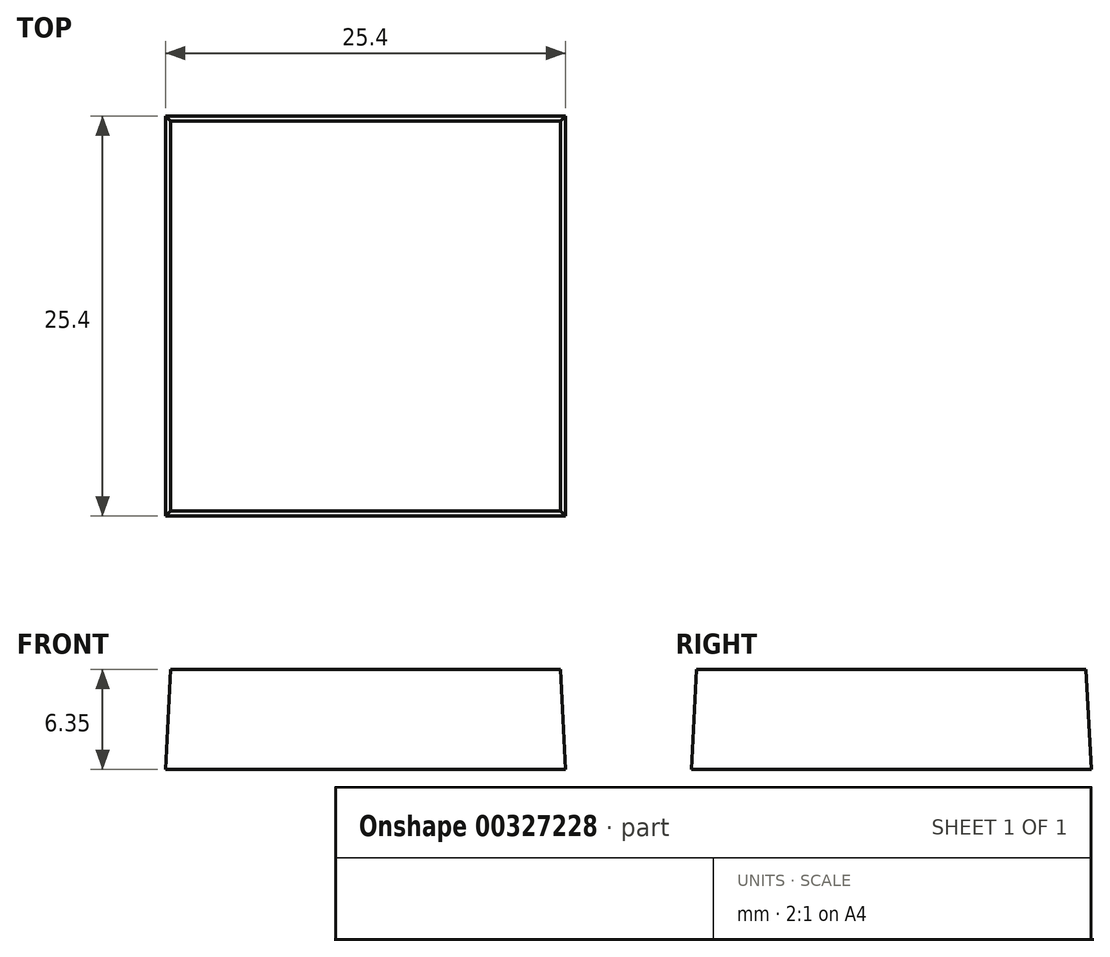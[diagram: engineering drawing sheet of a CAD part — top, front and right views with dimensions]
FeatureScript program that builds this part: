
annotation { "Feature Type Name" : "Feature", "Feature Type Description" : "" }
export const myFeature = defineFeature(function(context is Context, id is Id, definition is map)
    precondition{}
    {
        {
            var Q0;
            Q0=qCreatedBy(makeId("Top.planeOp"),FACE);
            var sketch = newSketch(context, id + "F0", { "sketchPlane" : qUnion([Q0])});
            skLineSegment(sketch, "E0.bottom", {"start": v(-12.7, 12.7) * mm, "end": v(12.7, 12.7) * mm});
            skLineSegment(sketch, "E0.top", {"start": v(-12.7, -12.7) * mm, "end": v(12.7, -12.7) * mm});
            skLineSegment(sketch, "E0.left", {"start": v(-12.7, 12.7) * mm, "end": v(-12.7, -12.7) * mm});
            skLineSegment(sketch, "E0.right", {"start": v(12.7, 12.7) * mm, "end": v(12.7, -12.7) * mm});
            skPoint(sketch, "E0.middle", {"position": v(0, 0) * mm});
            skSolve(sketch);
        }
        {
            var Q0;
            Q0 = qSketchRegion(id + "F0", true);
            extrude(context, id + "F1", {"entities" : qUnion([Q0]), "depth" : 6.35 * mm, "hasDraft" : true, "draftAngle" : 3 * degree, "draftPullDirection" : true});
        }
        {
            var Q0;
            Q0=qCreatedBy(makeId("Front.planeOp"),FACE);
            var sketch = newSketch(context, id + "F2", { "sketchPlane" : qUnion([Q0])});
            skArc(sketch, "E1", {"start": v(-10.16, 0) * mm, "mid": v(0, -23.56) * mm, "end": v(10.16, 0) * mm});
            skSolve(sketch);
        }
    });
